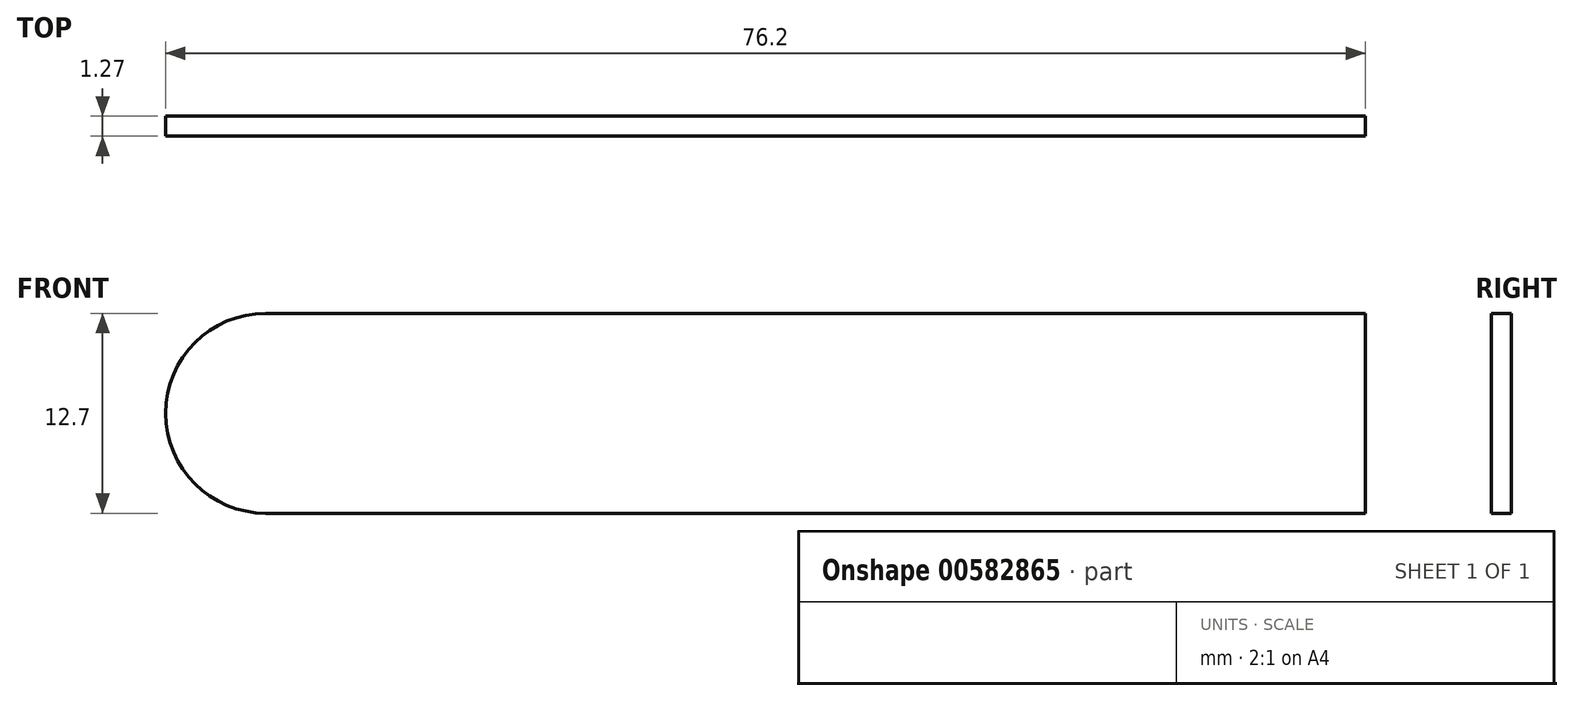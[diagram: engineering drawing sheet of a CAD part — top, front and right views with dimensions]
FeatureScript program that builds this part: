
annotation { "Feature Type Name" : "Feature", "Feature Type Description" : "" }
export const myFeature = defineFeature(function(context is Context, id is Id, definition is map)
    precondition{}
    {
        {
            var Q0;
            Q0=qCreatedBy(makeId("Front.planeOp"),FACE);
            var sketch = newSketch(context, id + "F0", { "sketchPlane" : qUnion([Q0])});
            skLineSegment(sketch, "E0.bottom", {"start": v(-42.57, 52.84) * mm, "end": v(27.28, 52.84) * mm});
            skLineSegment(sketch, "E0.top", {"start": v(-42.57, 40.14) * mm, "end": v(27.28, 40.14) * mm});
            skLineSegment(sketch, "E0.left", {"start": v(-48.92, 46.5) * mm, "end": v(-48.92, 46.5) * mm});
            skLineSegment(sketch, "E0.right", {"start": v(27.28, 52.84) * mm, "end": v(27.28, 40.14) * mm});
            skPoint(sketch, "E1.visualSharp", {"position": v(-48.92, 52.84) * mm});
            skArc(sketch, "E1.filletArc", {"start": v(-42.57, 52.84) * mm, "mid": v(-47.06, 50.98) * mm, "end": v(-48.92, 46.5) * mm});
            skPoint(sketch, "E2.visualSharp", {"position": v(-48.92, 40.14) * mm});
            skArc(sketch, "E2.filletArc", {"start": v(-48.92, 46.5) * mm, "mid": v(-47.06, 42) * mm, "end": v(-42.57, 40.14) * mm});
            skSolve(sketch);
        }
        {
            var Q0;
            Q0 = qSketchRegion(id + "F0", true);
            extrude(context, id + "F1", {"entities" : qUnion([Q0]), "depth" : 1.27 * mm, "offsetDistance" : 25.4 * mm});
        }
    });
